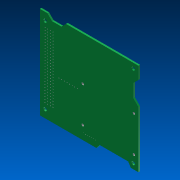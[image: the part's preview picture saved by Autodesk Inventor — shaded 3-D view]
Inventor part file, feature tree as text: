
AUTODESK INVENTOR PART (.ipt)
format: ipt  version: 2012 (Build 160160000, 160)  size: 580,096 bytes
history: native  units: in
note: dims shown in document units (in); Inventor stores cm internally (conversion verified against a paired STEP export)
features: other x2, sketch x1, extrude x1, imported_body x1
ambient origin geometry x8: Origin, YZ Plane, XZ Plane, XY Plane, X Axis, Y Axis, Z Axis, Center Point
feature tree (5):
  other  "Sólido1"
  other  "placa_pc1041"
  sketch  "Sketch3"  dims[d7=0.0315in d8=0.0in]
  extrude  "Extrusion2"  [1 undecoded]
  imported_body  "Base1"
note: 1 required parameter value undecoded (feature->parameter linkage not recoverable at this tier; creation-order binding heuristic only, values carry confidence <= 0.55)
